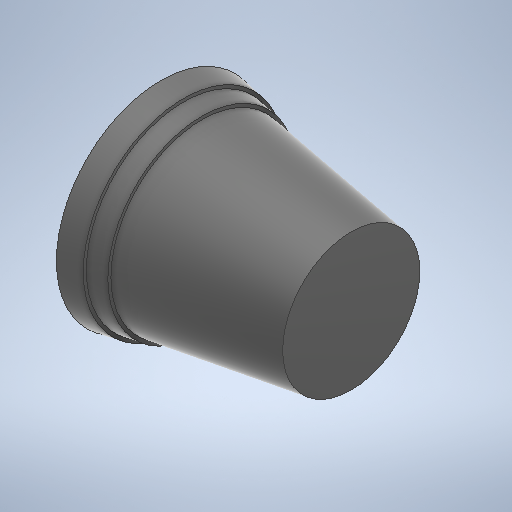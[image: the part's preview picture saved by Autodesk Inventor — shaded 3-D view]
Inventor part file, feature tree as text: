
AUTODESK INVENTOR PART (.ipt)
format: ipt  version: 2025.3 (Build 293356000, 356)  size: 298,496 bytes
history: native  units: mm
features: other x1, revolve x1, sketch x1
ambient origin geometry x8: Origin, YZ Plane, XZ Plane, XY Plane, X Axis, Y Axis, Z Axis, Center Point
bodies: Body1 (feature_tree)
feature tree (3):
  other  "Sólido1"
  revolve  "Revolución1"  [1 undecoded]
  sketch  "Boceto1"  dims[d0=900.0mm d1=1370.0mm d2=1250.0mm d3=17.453293mm d4=17.453293mm d5=150.0mm d6=20.0mm d7=120.0mm d8=20.0mm d9=20.0mm d11=17.453293mm d12=17.453293mm d13=20.0mm d14=20.0mm d15=20.0mm d18=20.0mm d19=25.0mm d20=90.0deg]
note: 1 required parameter value undecoded (feature->parameter linkage not recoverable at this tier; creation-order binding heuristic only, values carry confidence <= 0.55)
